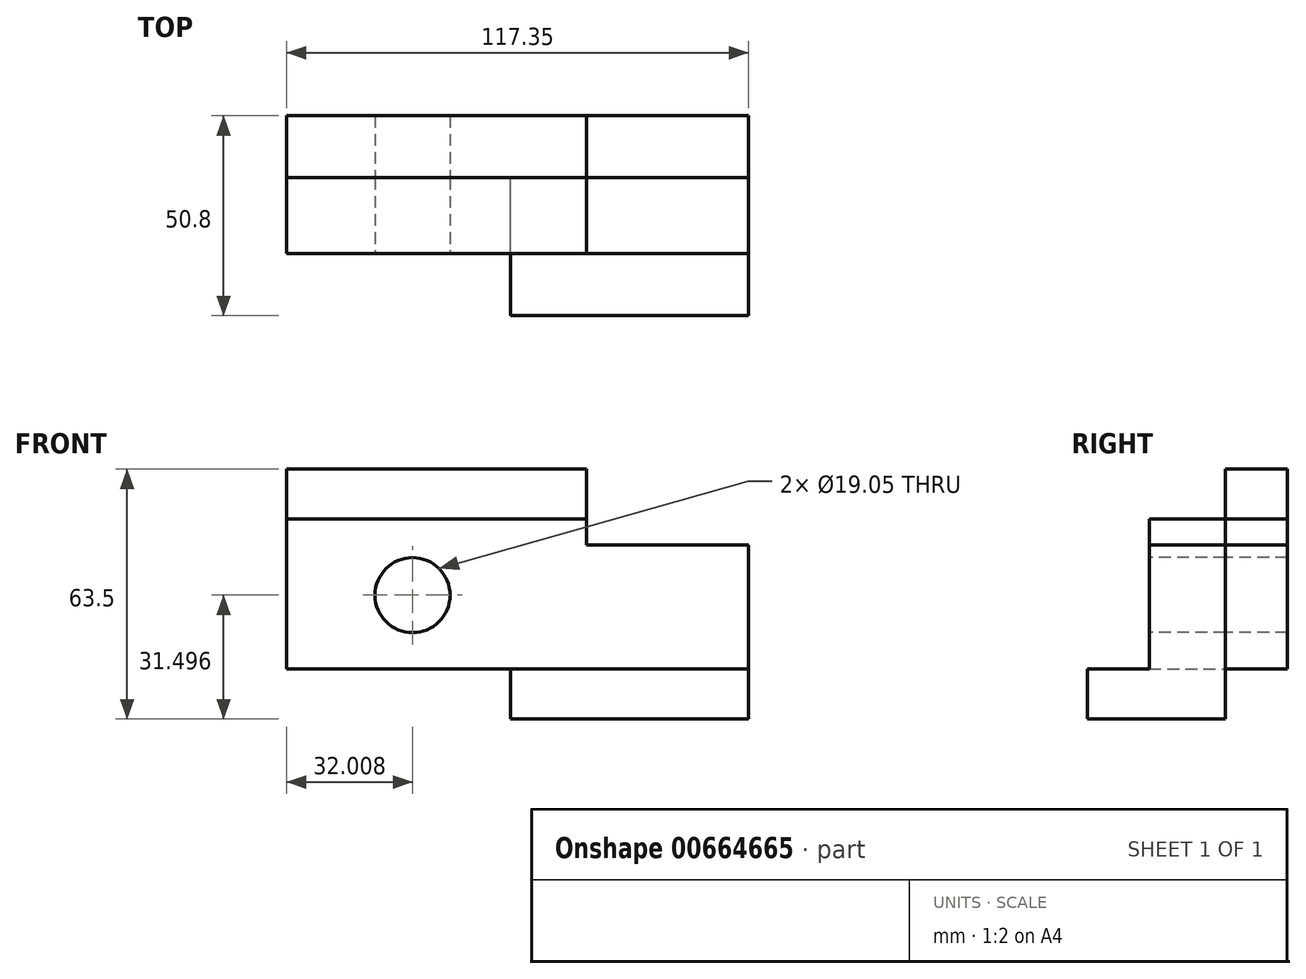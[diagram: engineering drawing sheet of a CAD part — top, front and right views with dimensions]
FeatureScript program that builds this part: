
annotation { "Feature Type Name" : "Feature", "Feature Type Description" : "" }
export const myFeature = defineFeature(function(context is Context, id is Id, definition is map)
    precondition{}
    {
        {
            var Q0;
            Q0=qCreatedBy(makeId("Front.planeOp"),FACE);
            var sketch = newSketch(context, id + "F0", { "sketchPlane" : qUnion([Q0])});
            skLineSegment(sketch, "E0", {"start": v(-56.9, 50.8) * mm, "end": v(19.3, 50.8) * mm});
            skLineSegment(sketch, "E1", {"start": v(19.3, 50.8) * mm, "end": v(19.3, 38.1) * mm});
            skLineSegment(sketch, "E2", {"start": v(19.3, 38.1) * mm, "end": v(-56.9, 38.1) * mm});
            skLineSegment(sketch, "E3", {"start": v(-56.9, 38.1) * mm, "end": v(-56.9, 50.8) * mm});
            skLineSegment(sketch, "E4", {"start": v(-56.9, 50.8) * mm, "end": v(-56.9, 38.1) * mm});
            skLineSegment(sketch, "E5", {"start": v(-56.9, 38.1) * mm, "end": v(-56.9, 0) * mm});
            skLineSegment(sketch, "E6", {"start": v(-56.9, 0) * mm, "end": v(60.45, 0) * mm});
            skLineSegment(sketch, "E7", {"start": v(60.45, 0) * mm, "end": v(60.45, 31.5) * mm});
            skLineSegment(sketch, "E8", {"start": v(60.45, 31.5) * mm, "end": v(19.3, 31.5) * mm});
            skLineSegment(sketch, "E9", {"start": v(19.3, 31.5) * mm, "end": v(19.3, 38.1) * mm});
            skLineSegment(sketch, "E10", {"start": v(60.45, 0) * mm, "end": v(60.45, -12.7) * mm});
            skLineSegment(sketch, "E11", {"start": v(60.45, -12.7) * mm, "end": v(0, -12.7) * mm});
            skLineSegment(sketch, "E12", {"start": v(0, -12.7) * mm, "end": v(0, 0) * mm});
            skSolve(sketch);
        }
        {
            var Q0;
            {var subQ0=sQuery(id+"F0.wireOp",EDGE,"E10");Q0=makeQuery(id+"F0.imprint","IMPRINT",FACE,{"disambiguationData":[TD([[makeQuery(id+"F0.imprint","IMPRINT",EDGE,{"derivedFrom":subQ0}),-1.0]])]});}
            extrude(context, id + "F1", {"entities" : qUnion([Q0]), "depth" : 35.05 * mm, "offsetDistance" : 25.4 * mm});
        }
        {
            var Q0;
            Q0=makeQuery(id+"F0.imprint","IMPRINT",FACE,{"disambiguationData":[TD([[makeQuery(id+"F0.imprint","IMPRINT",EDGE,{"derivedFrom":sQuery(id+"F0.wireOp",EDGE,"E0")}),-1.0]])]});
            extrude(context, id + "F2", {"entities" : qUnion([Q0]), "depth" : -15.75 * mm, "offsetDistance" : 25.4 * mm});
        }
        {
            var Q0;
            Q0=makeQuery(id+"F0.imprint","IMPRINT",FACE,{"disambiguationData":[TD([[makeQuery(id+"F0.imprint","IMPRINT",EDGE,{"derivedFrom":sQuery(id+"F0.wireOp",EDGE,"E2")}),1.0]])]});
            extrude(context, id + "F3", {"entities" : qUnion([Q0]), "operationType" : NewBodyOperationType.ADD, "depth" : 19.3 * mm, "offsetDistance" : 25.4 * mm});
        }
        {
            var Q0;
            Q0=makeQuery(id+"F0.imprint","IMPRINT",FACE,{"disambiguationData":[TD([[makeQuery(id+"F0.imprint","IMPRINT",EDGE,{"derivedFrom":sQuery(id+"F0.wireOp",EDGE,"E2")}),1.0]])]});
            extrude(context, id + "F4", {"entities" : qUnion([Q0]), "depth" : -15.75 * mm, "offsetDistance" : 25.4 * mm});
        }
        {
            var Q0;
            Q0=makeQuery(id+"F3.opExtrude","CAP_FACE",FACE,{"disambiguationData":[OSD([sQuery(id+"F0.wireOp",EDGE,"E2"),sQuery(id+"F0.wireOp",EDGE,"E5"),sQuery(id+"F0.wireOp",EDGE,"E6"),sQuery(id+"F0.wireOp",EDGE,"E7"),sQuery(id+"F0.wireOp",EDGE,"E8"),sQuery(id+"F0.wireOp",EDGE,"E9")])],"isStart":false});
            var sketch = newSketch(context, id + "F5", { "sketchPlane" : qUnion([Q0])});
            skCircle(sketch, "E13", {"center": v(-24.9, 18.8) * mm, "radius": 9.53 * mm});
            skSolve(sketch);
        }
        {
            var Q0;
            Q0=sQuery(id+"F5.wireOp",VERTEX,"E13.center");
            var Q1;
            Q1=makeQuery(id+"F1.opExtrude","SWEPT_BODY",BODY,{"disambiguationData":[OSD([sQuery(id+"F0.wireOp",EDGE,"E6"),sQuery(id+"F0.wireOp",EDGE,"E10"),sQuery(id+"F0.wireOp",EDGE,"E11"),sQuery(id+"F0.wireOp",EDGE,"E12")])]});
            var Q2;
            Q2=makeQuery(id+"F4.opExtrude","SWEPT_BODY",BODY,{"disambiguationData":[OSD([sQuery(id+"F0.wireOp",EDGE,"E2"),sQuery(id+"F0.wireOp",EDGE,"E5"),sQuery(id+"F0.wireOp",EDGE,"E6"),sQuery(id+"F0.wireOp",EDGE,"E7"),sQuery(id+"F0.wireOp",EDGE,"E8"),sQuery(id+"F0.wireOp",EDGE,"E9")])]});
            hole(context, id + "F6", {"style" : HoleStyle.SIMPLE, "endStyle" : HoleEndStyle.THROUGH, "holeDiameter" : 19.05 * mm, "majorDiameter" : 6.35 * mm, "isTappedThrough" : true, "tappedDepth" : 12.7 * mm, "tapClearance" : 3, "locations" : qUnion([Q0]), "scope" : qUnion([Q1, Q2])});
        }
    });
